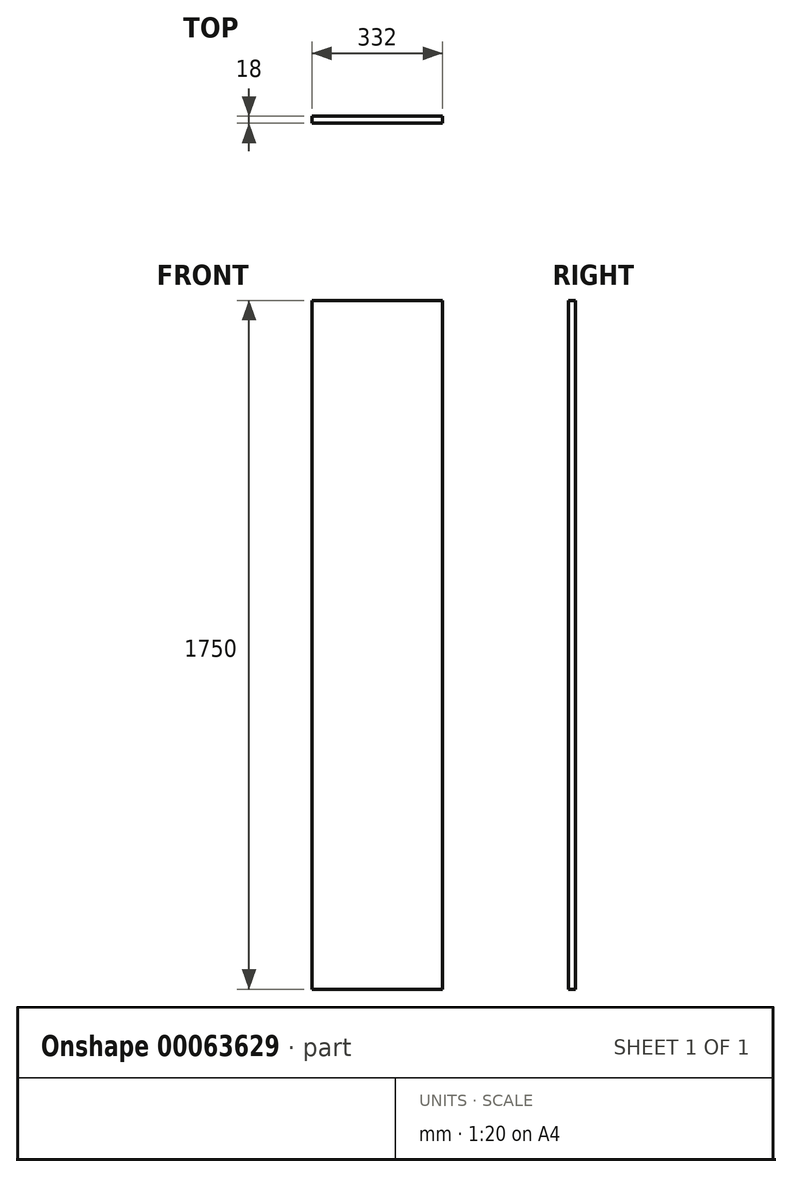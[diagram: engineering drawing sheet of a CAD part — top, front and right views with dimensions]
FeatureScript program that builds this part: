
annotation { "Feature Type Name" : "Feature", "Feature Type Description" : "" }
export const myFeature = defineFeature(function(context is Context, id is Id, definition is map)
    precondition{}
    {
        {
            var Q0;
            Q0=qCreatedBy(makeId("Front.planeOp"),FACE);
            var sketch = newSketch(context, id + "F0", { "sketchPlane" : qUnion([Q0])});
            skLineSegment(sketch, "E0.bottom", {"start": v(0, 0) * mm, "end": v(332, 0) * mm});
            skLineSegment(sketch, "E0.top", {"start": v(0, -1750) * mm, "end": v(332, -1750) * mm});
            skLineSegment(sketch, "E0.left", {"start": v(0, 0) * mm, "end": v(0, -1750) * mm});
            skLineSegment(sketch, "E0.right", {"start": v(332, 0) * mm, "end": v(332, -1750) * mm});
            skSolve(sketch);
        }
        {
            var Q0;
            Q0 = qSketchRegion(id + "F0", true);
            extrude(context, id + "F1", {"entities" : qUnion([Q0]), "depth" : 18 * mm});
        }
    });
